# Revit family: LTC-3SQD
name_source: partatom
category: Lighting Fixtures
units: mm (PartAtom-declared; Revit-internal decimal feet)

## family parameters
Cut with Voids When Loaded = No
Host = Face
Light Source = Yes
OmniClass Number = 23.80.70.11.14.11
OmniClass Title = Downlights
Part Type = Normal
Room Calculation Point = No
Round Connector Dimension = Use Diameter
Shared = Yes

## types (1)
- LTC-3SQD-S
    Apparent Load = 52 VA
    Ceiling Cutout = 6 1/2"
    Color Filter = 16777215
    Connector Description = Lighting Connector
    Cutout Radius = 3"
    Default Elevation = 48"
    Description = LITEISTRY™ 3inch Square Cylinder Downlight
    Dimming Lamp Color Temperature Shift = <None>
    Emit Shape Visible in Rendering = Yes
    Emit from Rectangle Length = 4"
    Emit from Rectangle Width = 4"
    Frequency = 60 Hz
    Glass = White Glass
    Is 120V = Yes
    Is 277V = No
    Lamp = LED's
    Load Classification = Lighting
    Manufacturer = Prescolite
    Model = LTC-3SQD
    Photometric Notes = More IES files download on Photometric Web Link
    Photometric Web File = LTC-3SQD-P-20L35K8MD-DM1-S-BL.ies
    Product Material = Paint - Carbon Black
    Reflector Finish = Paint - Carbon Black
    Tilt Angle = -90.00°
    URL = https://www.currentlighting.com
    Voltage = 120 V
    Wattage Comments = 8-25

## geometry (parser evidence)
native form markers: Blend x4, Sweep x3
no freeform markers — native parametric forms only
